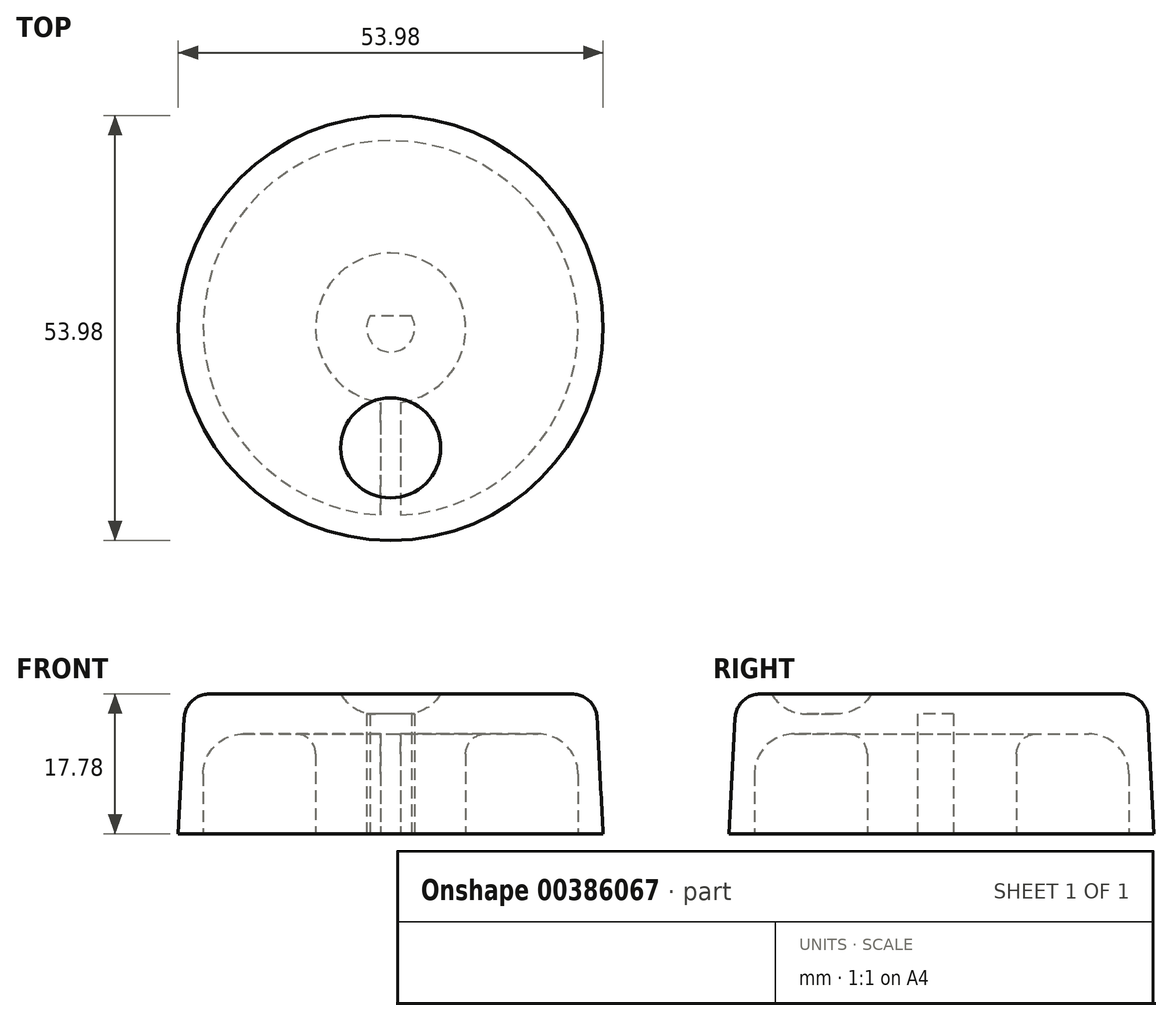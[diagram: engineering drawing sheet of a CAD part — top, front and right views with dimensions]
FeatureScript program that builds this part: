
annotation { "Feature Type Name" : "Feature", "Feature Type Description" : "" }
export const myFeature = defineFeature(function(context is Context, id is Id, definition is map)
    precondition{}
    {
        {
            var Q0;
            Q0=qCreatedBy(makeId("Top.planeOp"),FACE);
            var sketch = newSketch(context, id + "F0", { "sketchPlane" : qUnion([Q0])});
            skCircle(sketch, "E0", {"center": v(0, 0) * mm, "radius": 26.99 * mm});
            skSolve(sketch);
        }
        {
            var Q0;
            Q0 = qSketchRegion(id + "F0", true);
            extrude(context, id + "F1", {"entities" : qUnion([Q0]), "depth" : 17.78 * mm, "hasDraft" : true, "draftAngle" : 3 * degree, "draftPullDirection" : true});
        }
        {
            var Q0;
            Q0=makeQuery(id+"F1.opExtrude","CAP_EDGE",EDGE,{"disambiguationData":[OSD([sQuery(id+"F0.wireOp",EDGE,"E0")])],"isStart":false});
            fillet(context, id + "F2", {"entities" : qUnion([Q0]), "radius" : 3.17 * mm, "tangentPropagation" : true, "allowEdgeOverflow" : false});
        }
        {
            var Q0;
            Q0=makeQuery(id+"F1.opExtrude","CAP_FACE",FACE,{"disambiguationData":[OSD([sQuery(id+"F0.wireOp",EDGE,"E0")])],"isStart":false});
            var sketch = newSketch(context, id + "F3", { "sketchPlane" : qUnion([Q0])});
            skCircle(sketch, "E1", {"center": v(0, -15.24) * mm, "radius": 6.35 * mm});
            skSolve(sketch);
        }
        {
            var Q0;
            Q0 = qSketchRegion(id + "F3", true);
            extrude(context, id + "F4", {"entities" : qUnion([Q0]), "operationType" : NewBodyOperationType.REMOVE, "oppositeDirection" : true, "depth" : 2.54 * mm});
        }
        {
            var Q0;
            Q0=makeQuery(id+"F4.boolean.opBoolean","COPY",FACE,{"derivedFrom":makeQuery(id+"F4.opExtrude","CAP_FACE",FACE,{"disambiguationData":[OSD([sQuery(id+"F3.wireOp",EDGE,"E1")])],"isStart":false})});
            fillet(context, id + "F5", {"entities" : qUnion([Q0]), "radius" : 5.08 * mm, "tangentPropagation" : true, "allowEdgeOverflow" : false});
        }
        {
            var Q0;
            Q0=makeQuery(id+"F1.opExtrude","CAP_FACE",FACE,{"disambiguationData":[OSD([sQuery(id+"F0.wireOp",EDGE,"E0")])],"isStart":true});
            var sketch = newSketch(context, id + "F6", { "sketchPlane" : qUnion([Q0])});
            skCircle(sketch, "E2.0", {"center": v(0, 15.24) * mm, "radius": 1.95 * mm, "construction": true});
            skCircle(sketch, "E2.1", {"center": v(0, 15.24) * mm, "radius": 6.35 * mm, "construction": true});
            skArc(sketch, "E3", {"start": v(-1.27, 9.44) * mm, "mid": v(0, -9.53) * mm, "end": v(1.27, 9.44) * mm});
            skArc(sketch, "E4", {"start": v(-1.27, 23.78) * mm, "mid": v(0, -23.81) * mm, "end": v(1.27, 23.78) * mm});
            skLineSegment(sketch, "E5", {"start": v(1.27, 9.44) * mm, "end": v(1.27, 23.78) * mm});
            skLineSegment(sketch, "E6", {"start": v(-1.27, 9.44) * mm, "end": v(-1.27, 23.78) * mm});
            skPoint(sketch, "E7.orphan", {"position": v(-1.27, 0) * mm});
            skPoint(sketch, "E8.orphan", {"position": v(1.27, 0) * mm});
            skSolve(sketch);
        }
        {
            var Q0;
            Q0 = qSketchRegion(id + "F6", true);
            extrude(context, id + "F7", {"entities" : qUnion([Q0]), "operationType" : NewBodyOperationType.REMOVE, "oppositeDirection" : true, "depth" : 12.7 * mm});
        }
        {
            var Q0;
            Q0=makeQuery(id+"F7.boolean.opBoolean","COPY",EDGE,{"derivedFrom":makeQuery(id+"F7.opExtrude","CAP_EDGE",EDGE,{"disambiguationData":[OSD([sQuery(id+"F6.wireOp",EDGE,"E4")])],"isStart":false})});
            fillet(context, id + "F8", {"entities" : qUnion([Q0]), "radius" : 5.08 * mm, "tangentPropagation" : true, "allowEdgeOverflow" : false});
        }
        {
            var Q0;
            Q0=makeQuery(id+"F7.boolean.opBoolean","COPY",EDGE,{"derivedFrom":makeQuery(id+"F7.opExtrude","CAP_EDGE",EDGE,{"disambiguationData":[OSD([sQuery(id+"F6.wireOp",EDGE,"E3")])],"isStart":false})});
            fillet(context, id + "F9", {"entities" : qUnion([Q0]), "radius" : 2.54 * mm, "tangentPropagation" : true, "allowEdgeOverflow" : false});
        }
        {
            var Q0;
            Q0=makeQuery(id+"F1.opExtrude","CAP_FACE",FACE,{"disambiguationData":[OSD([sQuery(id+"F0.wireOp",EDGE,"E0")])],"isStart":true});
            var sketch = newSketch(context, id + "F10", { "sketchPlane" : qUnion([Q0])});
            skArc(sketch, "E9", {"start": v(2.64, -1.52) * mm, "mid": v(0, 3.05) * mm, "end": v(-2.64, -1.52) * mm});
            skLineSegment(sketch, "E10", {"start": v(2.64, -1.52) * mm, "end": v(-2.64, -1.52) * mm});
            skSolve(sketch);
        }
        {
            var Q0;
            Q0 = qSketchRegion(id + "F10", true);
            extrude(context, id + "F11", {"entities" : qUnion([Q0]), "operationType" : NewBodyOperationType.REMOVE, "oppositeDirection" : true, "depth" : 15.24 * mm});
        }
    });
